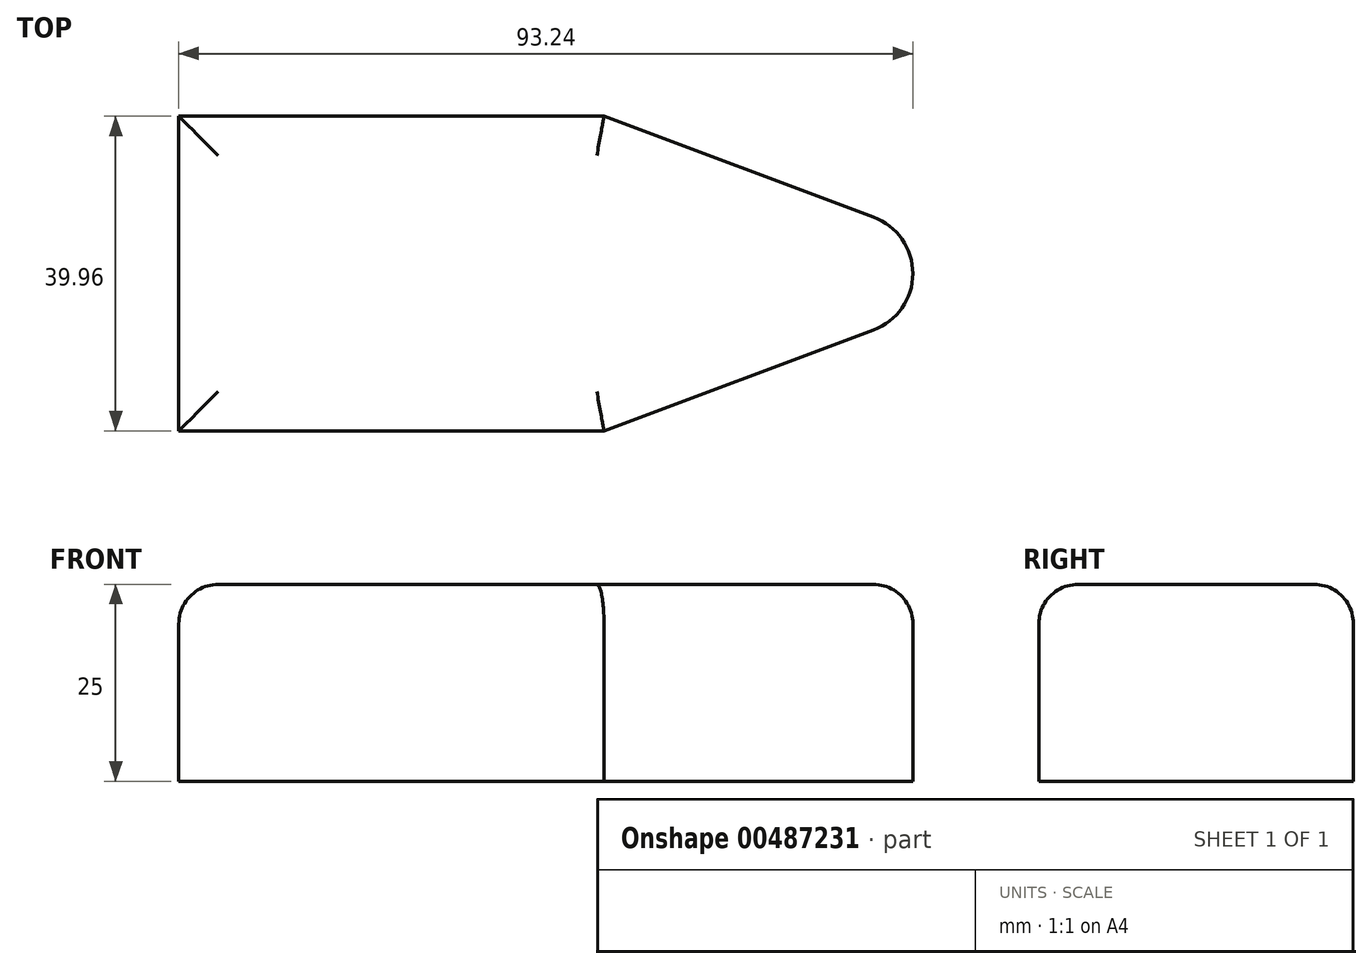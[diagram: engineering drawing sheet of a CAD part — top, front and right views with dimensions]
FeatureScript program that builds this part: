
annotation { "Feature Type Name" : "Feature", "Feature Type Description" : "" }
export const myFeature = defineFeature(function(context is Context, id is Id, definition is map)
    precondition{}
    {
        {
            var Q0;
            Q0=qCreatedBy(makeId("Top.planeOp"),FACE);
            var sketch = newSketch(context, id + "F0", { "sketchPlane" : qUnion([Q0])});
            skLineSegment(sketch, "E0.bottom", {"start": v(27, -19.98) * mm, "end": v(-27, -19.98) * mm});
            skLineSegment(sketch, "E0.top", {"start": v(27, 19.98) * mm, "end": v(-27, 19.98) * mm});
            skLineSegment(sketch, "E0.left", {"start": v(27, -19.98) * mm, "end": v(27, 19.98) * mm});
            skLineSegment(sketch, "E0.right", {"start": v(-27, -19.98) * mm, "end": v(-27, 19.98) * mm});
            skPoint(sketch, "E0.middle", {"position": v(0, 0) * mm});
            skCircle(sketch, "E1", {"center": v(58.58, 0) * mm, "radius": 7.66 * mm});
            skLineSegment(sketch, "E2", {"start": v(27, 19.98) * mm, "end": v(61.26, 7.18) * mm});
            skLineSegment(sketch, "E3", {"start": v(27, -19.98) * mm, "end": v(61.26, -7.18) * mm});
            skSolve(sketch);
        }
        {
            var Q0;
            Q0=makeQuery(id+"F0.imprint","IMPRINT",FACE,{"disambiguationData":[TD([[makeQuery(id+"F0.imprint","IMPRINT",EDGE,{"derivedFrom":sQuery(id+"F0.wireOp",EDGE,"E0.bottom")}),-1.0]])]});
            var Q1;
            Q1=makeQuery(id+"F0.imprint","IMPRINT",FACE,{"disambiguationData":[TD([[makeQuery(id+"F0.imprint","IMPRINT",EDGE,{"derivedFrom":sQuery(id+"F0.wireOp",EDGE,"E0.left")}),-1.0]])]});
            var Q2;
            {var subQ0=sQuery(id+"F0.wireOp",EDGE,"E1");var subQ1=makeQuery(id+"F0.imprint","INTERSECT",VERTEX,{"derivedFrom":[subQ0,sQuery(id+"F0.wireOp",EDGE,"E2")]});Q2=makeQuery(id+"F0.imprint","IMPRINT",FACE,{"disambiguationData":[TD([[makeQuery(id+"F0.imprint","IMPRINT",EDGE,{"disambiguationData":[TD([[subQ1,-1.0]])],"derivedFrom":subQ0}),1.0]])]});}
            extrude(context, id + "F1", {"entities" : qUnion([Q0, Q1, Q2]), "depth" : 25 * mm, "offsetDistance" : 25 * mm});
        }
        {
            var Q0;
            Q0=makeQuery(id+"F1.opExtrude","CAP_EDGE",EDGE,{"disambiguationData":[OSD([sQuery(id+"F0.wireOp",EDGE,"E0.bottom")])],"isStart":false});
            var Q1;
            Q1=makeQuery(id+"F1.opExtrude","CAP_EDGE",EDGE,{"disambiguationData":[OSD([sQuery(id+"F0.wireOp",EDGE,"E0.right")])],"isStart":false});
            var Q2;
            Q2=makeQuery(id+"F1.opExtrude","CAP_EDGE",EDGE,{"disambiguationData":[OSD([sQuery(id+"F0.wireOp",EDGE,"E0.top")])],"isStart":false});
            var Q3;
            Q3=makeQuery(id+"F1.opExtrude","CAP_EDGE",EDGE,{"disambiguationData":[OSD([sQuery(id+"F0.wireOp",EDGE,"E2")])],"isStart":false});
            var Q4;
            Q4=makeQuery(id+"F1.opExtrude","CAP_EDGE",EDGE,{"disambiguationData":[OSD([sQuery(id+"F0.wireOp",EDGE,"E1")])],"isStart":false});
            var Q5;
            Q5=makeQuery(id+"F1.opExtrude","CAP_EDGE",EDGE,{"disambiguationData":[OSD([sQuery(id+"F0.wireOp",EDGE,"E3")])],"isStart":false});
            fillet(context, id + "F2", {"entities" : qUnion([Q0, Q1, Q2, Q3, Q4, Q5]), "radius" : 5 * mm, "tangentPropagation" : true, "allowEdgeOverflow" : false});
        }
    });
